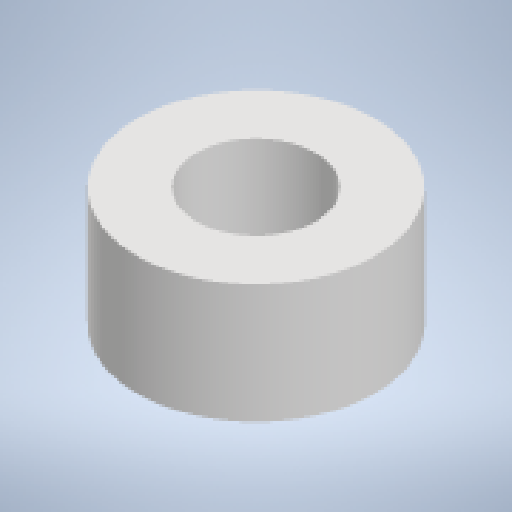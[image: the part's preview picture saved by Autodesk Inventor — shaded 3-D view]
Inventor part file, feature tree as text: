
AUTODESK INVENTOR PART (.ipt)
format: ipt  version: 2024.2 (Build 282272000, 272)  size: 110,592 bytes
history: native  units: mm
features: other x1, extrude x1, sketch x1
ambient origin geometry x8: Origin, YZ Plane, XZ Plane, XY Plane, X Axis, Y Axis, Z Axis, Center Point
bodies: Body1 (feature_tree)
feature tree (3):
  other  "Твердое тело1"
  extrude  "Выдавливание1"  Depth=5.0mm
  sketch  "Эскиз1"
